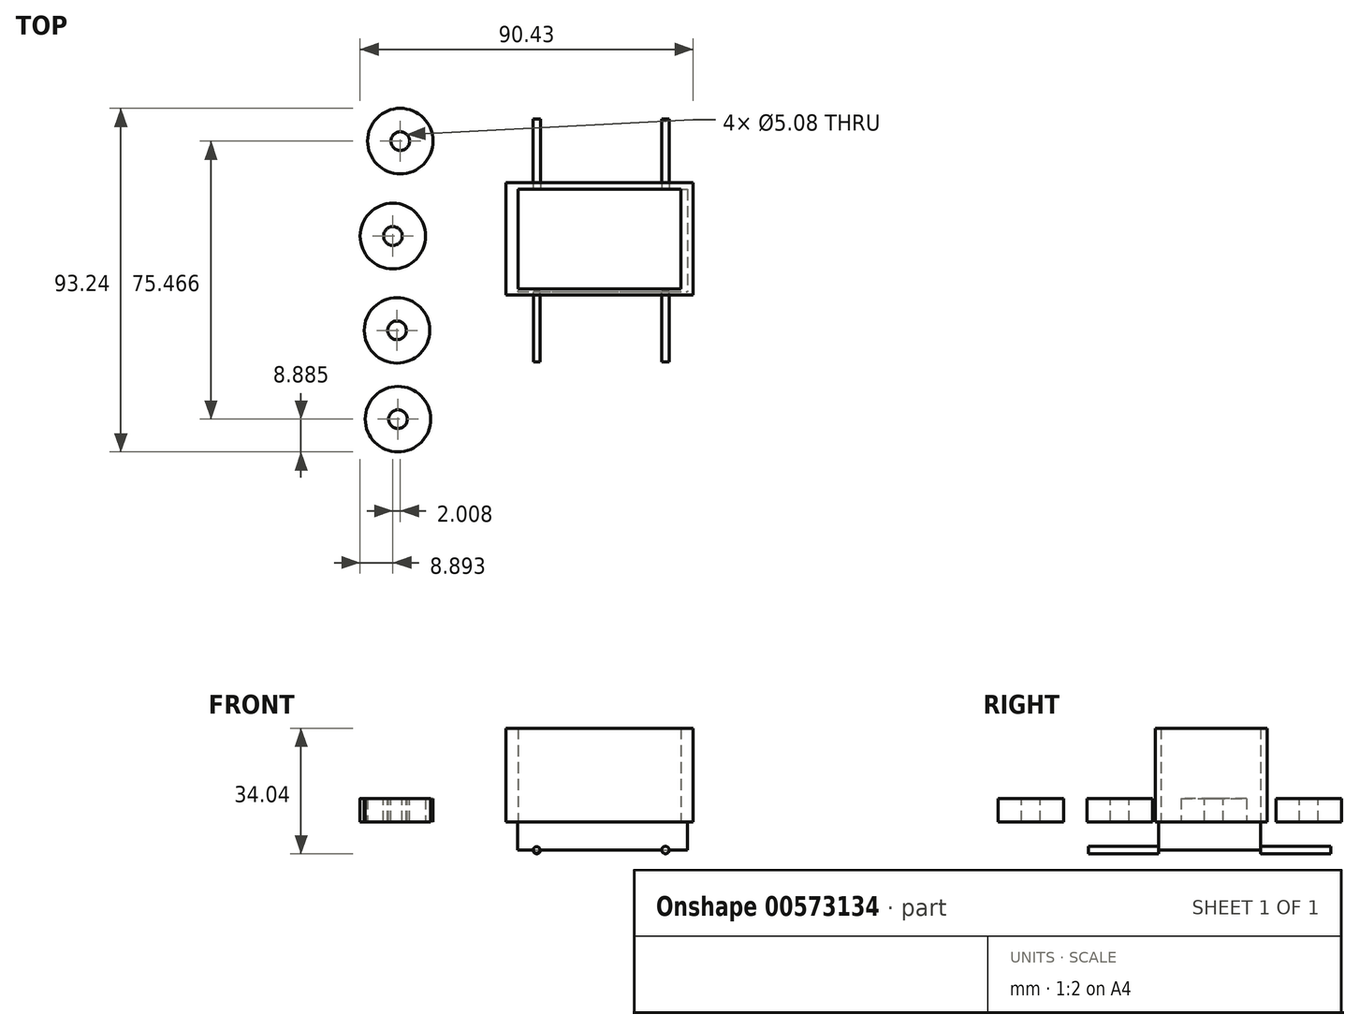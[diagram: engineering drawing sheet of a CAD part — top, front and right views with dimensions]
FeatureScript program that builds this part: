
annotation { "Feature Type Name" : "Feature", "Feature Type Description" : "" }
export const myFeature = defineFeature(function(context is Context, id is Id, definition is map)
    precondition{}
    {
        {
            var Q0;
            Q0=qCreatedBy(makeId("Top.planeOp"),FACE);
            var sketch = newSketch(context, id + "F0", { "sketchPlane" : qUnion([Q0])});
            skLineSegment(sketch, "E0.bottom", {"start": v(0, 0) * mm, "end": v(-1.27, 0) * mm});
            skLineSegment(sketch, "E1.right", {"start": v(-1.27, 0) * mm, "end": v(-1.27, -1.22) * mm});
            skLineSegment(sketch, "E2.bottom", {"start": v(-16.65, 19.04) * mm, "end": v(34.15, 19.04) * mm});
            skLineSegment(sketch, "E2.top", {"start": v(-16.65, 17.3) * mm, "end": v(34.15, 17.3) * mm});
            skLineSegment(sketch, "E2.left", {"start": v(-16.65, 19.04) * mm, "end": v(-16.65, 17.3) * mm});
            skLineSegment(sketch, "E2.right", {"start": v(34.15, 19.04) * mm, "end": v(34.15, 17.3) * mm});
            skLineSegment(sketch, "E3.bottom", {"start": v(34.15, 17.3) * mm, "end": v(30.74, 17.3) * mm});
            skLineSegment(sketch, "E3.top", {"start": v(34.15, -9.81) * mm, "end": v(30.74, -9.81) * mm});
            skLineSegment(sketch, "E3.left", {"start": v(34.15, 17.3) * mm, "end": v(34.15, -9.81) * mm});
            skLineSegment(sketch, "E3.right", {"start": v(30.74, 17.3) * mm, "end": v(30.74, -9.81) * mm});
            skLineSegment(sketch, "E4.bottom", {"start": v(34.15, -9.81) * mm, "end": v(-16.65, -9.81) * mm});
            skLineSegment(sketch, "E4.top", {"start": v(34.15, -11.39) * mm, "end": v(-16.65, -11.39) * mm});
            skLineSegment(sketch, "E4.left", {"start": v(34.15, -9.81) * mm, "end": v(34.15, -11.39) * mm});
            skLineSegment(sketch, "E4.right", {"start": v(-16.65, -9.81) * mm, "end": v(-16.65, -11.39) * mm});
            skLineSegment(sketch, "E5.bottom", {"start": v(-16.65, -9.81) * mm, "end": v(-13.4, -9.81) * mm});
            skLineSegment(sketch, "E5.top", {"start": v(-16.65, 17.3) * mm, "end": v(-13.4, 17.3) * mm});
            skLineSegment(sketch, "E5.left", {"start": v(-16.65, -9.81) * mm, "end": v(-16.65, 17.3) * mm});
            skLineSegment(sketch, "E5.right", {"start": v(-13.4, -9.81) * mm, "end": v(-13.4, 17.3) * mm});
            skSolve(sketch);
        }
        {
            var Q0;
            Q0 = qSketchRegion(id + "F0", true);
            extrude(context, id + "F1", {"entities" : qUnion([Q0]), "depth" : 25.4 * mm, "offsetDistance" : 25.4 * mm});
        }
        {
            var Q0;
            Q0 = qSketchRegion(id + "F0", true);
            extrude(context, id + "F2", {"entities" : qUnion([Q0]), "operationType" : NewBodyOperationType.ADD, "depth" : 25.4 * mm, "offsetDistance" : 25.4 * mm});
        }
        {
            var Q0;
            Q0=qCreatedBy(makeId("Top.planeOp"),FACE);
            var sketch = newSketch(context, id + "F3", { "sketchPlane" : qUnion([Q0])});
            skLineSegment(sketch, "E6.bottom", {"start": v(-13.5, 17.28) * mm, "end": v(32.62, 17.28) * mm});
            skLineSegment(sketch, "E6.top", {"start": v(-13.5, -10.49) * mm, "end": v(32.62, -10.49) * mm});
            skLineSegment(sketch, "E6.left", {"start": v(-13.5, 17.28) * mm, "end": v(-13.5, -10.49) * mm});
            skLineSegment(sketch, "E6.right", {"start": v(32.62, 17.28) * mm, "end": v(32.62, -10.49) * mm});
            skSolve(sketch);
        }
        {
            var Q0;
            Q0 = qSketchRegion(id + "F3", true);
            extrude(context, id + "F4", {"entities" : qUnion([Q0]), "operationType" : NewBodyOperationType.ADD, "depth" : -7.62 * mm, "offsetDistance" : 25.4 * mm});
        }
        {
            var Q0;
            Q0=makeQuery(id+"F4.opExtrude","SWEPT_FACE",FACE,{"disambiguationData":[OSD([sQuery(id+"F3.wireOp",EDGE,"E6.bottom")])]});
            var sketch = newSketch(context, id + "F5", { "sketchPlane" : qUnion([Q0])});
            skCircle(sketch, "E7", {"center": v(-26.61, -7.62) * mm, "radius": 1.02 * mm});
            skCircle(sketch, "E8", {"center": v(8.34, -7.62) * mm, "radius": 1.02 * mm});
            skSolve(sketch);
        }
        {
            var Q0;
            Q0 = qSketchRegion(id + "F5", true);
            extrude(context, id + "F6", {"entities" : qUnion([Q0]), "operationType" : NewBodyOperationType.ADD, "depth" : 19.05 * mm, "offsetDistance" : 25.4 * mm});
        }
        {
            var Q0;
            Q0=makeQuery(id+"F4.opExtrude","SWEPT_FACE",FACE,{"disambiguationData":[OSD([sQuery(id+"F3.wireOp",EDGE,"E6.top")])]});
            var sketch = newSketch(context, id + "F7", { "sketchPlane" : qUnion([Q0])});
            skCircle(sketch, "E9", {"center": v(-8.37, -7.62) * mm, "radius": 0.9 * mm});
            skCircle(sketch, "E10", {"center": v(26.58, -7.62) * mm, "radius": 1 * mm});
            skSolve(sketch);
        }
        {
            var Q0;
            Q0 = qSketchRegion(id + "F7", true);
            extrude(context, id + "F8", {"entities" : qUnion([Q0]), "operationType" : NewBodyOperationType.ADD, "depth" : 19.05 * mm, "offsetDistance" : 25.4 * mm});
        }
        {
            var Q0;
            Q0=qCreatedBy(makeId("Top.planeOp"),FACE);
            var sketch = newSketch(context, id + "F9", { "sketchPlane" : qUnion([Q0])});
            skCircle(sketch, "E11", {"center": v(-45.38, 30.33) * mm, "radius": 8.9 * mm});
            skCircle(sketch, "E12", {"center": v(-47.39, 4.56) * mm, "radius": 8.9 * mm});
            skCircle(sketch, "E13", {"center": v(-46.27, -21.03) * mm, "radius": 8.9 * mm});
            skCircle(sketch, "E14", {"center": v(-46, -45.13) * mm, "radius": 8.9 * mm});
            skSolve(sketch);
        }
        {
            var Q0;
            Q0 = qSketchRegion(id + "F9", true);
            extrude(context, id + "F10", {"entities" : qUnion([Q0]), "depth" : 6.35 * mm, "offsetDistance" : 25.4 * mm});
        }
        {
            var Q0;
            Q0=makeQuery(id+"F10.opExtrude","CAP_FACE",FACE,{"disambiguationData":[OSD([sQuery(id+"F9.wireOp",EDGE,"E11")])],"isStart":false});
            var sketch = newSketch(context, id + "F11", { "sketchPlane" : qUnion([Q0])});
            skCircle(sketch, "E15", {"center": v(-45.38, 30.33) * mm, "radius": 2.54 * mm});
            skSolve(sketch);
        }
        {
            var Q0;
            Q0 = qSketchRegion(id + "F11", true);
            extrude(context, id + "F12", {"entities" : qUnion([Q0]), "operationType" : NewBodyOperationType.REMOVE, "oppositeDirection" : true, "depth" : 25.4 * mm, "offsetDistance" : 25.4 * mm});
        }
        {
            var Q0;
            Q0=makeQuery(id+"F10.opExtrude","CAP_FACE",FACE,{"disambiguationData":[OSD([sQuery(id+"F9.wireOp",EDGE,"E12")])],"isStart":false});
            var sketch = newSketch(context, id + "F13", { "sketchPlane" : qUnion([Q0])});
            skCircle(sketch, "E16", {"center": v(-47.39, 4.56) * mm, "radius": 2.54 * mm});
            skSolve(sketch);
        }
        {
            var Q0;
            Q0 = qSketchRegion(id + "F13", true);
            extrude(context, id + "F14", {"entities" : qUnion([Q0]), "operationType" : NewBodyOperationType.REMOVE, "oppositeDirection" : true, "depth" : 25.4 * mm, "offsetDistance" : 25.4 * mm});
        }
        {
            var Q0;
            Q0=makeQuery(id+"F10.opExtrude","CAP_FACE",FACE,{"disambiguationData":[OSD([sQuery(id+"F9.wireOp",EDGE,"E13")])],"isStart":false});
            var sketch = newSketch(context, id + "F15", { "sketchPlane" : qUnion([Q0])});
            skCircle(sketch, "E17", {"center": v(-46.27, -21.03) * mm, "radius": 2.54 * mm});
            skSolve(sketch);
        }
        {
            var Q0;
            Q0 = qSketchRegion(id + "F15", true);
            extrude(context, id + "F16", {"entities" : qUnion([Q0]), "operationType" : NewBodyOperationType.REMOVE, "oppositeDirection" : true, "depth" : 25.4 * mm, "offsetDistance" : 25.4 * mm});
        }
        {
            var Q0;
            Q0=makeQuery(id+"F10.opExtrude","CAP_FACE",FACE,{"disambiguationData":[OSD([sQuery(id+"F9.wireOp",EDGE,"E14")])],"isStart":false});
            var sketch = newSketch(context, id + "F17", { "sketchPlane" : qUnion([Q0])});
            skCircle(sketch, "E18", {"center": v(-46, -45.13) * mm, "radius": 2.54 * mm});
            skSolve(sketch);
        }
        {
            var Q0;
            Q0 = qSketchRegion(id + "F17", true);
            extrude(context, id + "F18", {"entities" : qUnion([Q0]), "operationType" : NewBodyOperationType.REMOVE, "oppositeDirection" : true, "depth" : 25.4 * mm, "offsetDistance" : 25.4 * mm});
        }
    });
